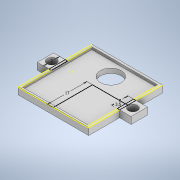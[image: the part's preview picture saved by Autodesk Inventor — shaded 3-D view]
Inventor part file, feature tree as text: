
AUTODESK INVENTOR PART (.ipt)
format: ipt  version: 2020.2 (Build 242310000, 310)  size: 188,416 bytes
history: native  units: in
note: dims shown in document units (in); Inventor stores cm internally (conversion verified against a paired STEP export)
features: sketch x7, extrude x4, hole x2, projected_geometry x1
ambient origin geometry x8: Origin, YZ Plane, XZ Plane, XY Plane, X Axis, Y Axis, Z Axis, Center Point
bodies: Solid1 (feature_tree)
feature tree (14):
  extrude  "Extrusion1"  Depth=1.2in
  extrude  "Extrusion3"  Depth=0.0394in
  hole  "Hole1"  [1 undecoded]
  sketch  "Sketch5"  dims[d7=0.0394in d10=0.0394in d11=0.0in]
  extrude  "Extrusion5"  Depth=0.0394in TaperAngle=0.0deg
  hole  "Hole2"  [1 undecoded]
  extrude  "Extrusion6"  Depth=0.2756in
  sketch  "Sketch1"  dims[d0=1.2in d1=1.2598in]
  sketch  "Sketch3"  dims[d2=0.0787in d3=0.0in d4=0.0394in]
  sketch  "Sketch4"  dims[d5=0.0394in d6=1.1811in]
  sketch  "Sketch6"  dims[d12=0.2756in]
  sketch  "Sketch7"  dims[d13=0.3543in d14=0.2362in d15=0.225in d16=0.0787in d17=0.5635in d18=0.315in d19=0.8108in d20=0.6693in]
  sketch  "Sketch8"  dims[d21=0.1378in d22=0.2756in d23=0.2756in d26=0.1969in d27=0.1969in d28=0.1181in d29=0.0in d30=0.6693in d31=0.689in d32=1.378in d33=0.1575in d34=0.2362in d35=0.225in d36=0.0787in d37=0.5635in d38=0.315in d39=0.8108in d40=0.0079in d41=0.0in d42=0.0394in d43=0.0059in d44=0.0098in d45=0.0148in d46=0.5635in d47=0.0295in d48=0.8108in d49=0.0025in d50=0.0295in d51=0.0148in]
  projected_geometry  "Projected Loop2"
note: 2 required parameter values undecoded (feature->parameter linkage not recoverable at this tier; creation-order binding heuristic only, values carry confidence <= 0.55)
